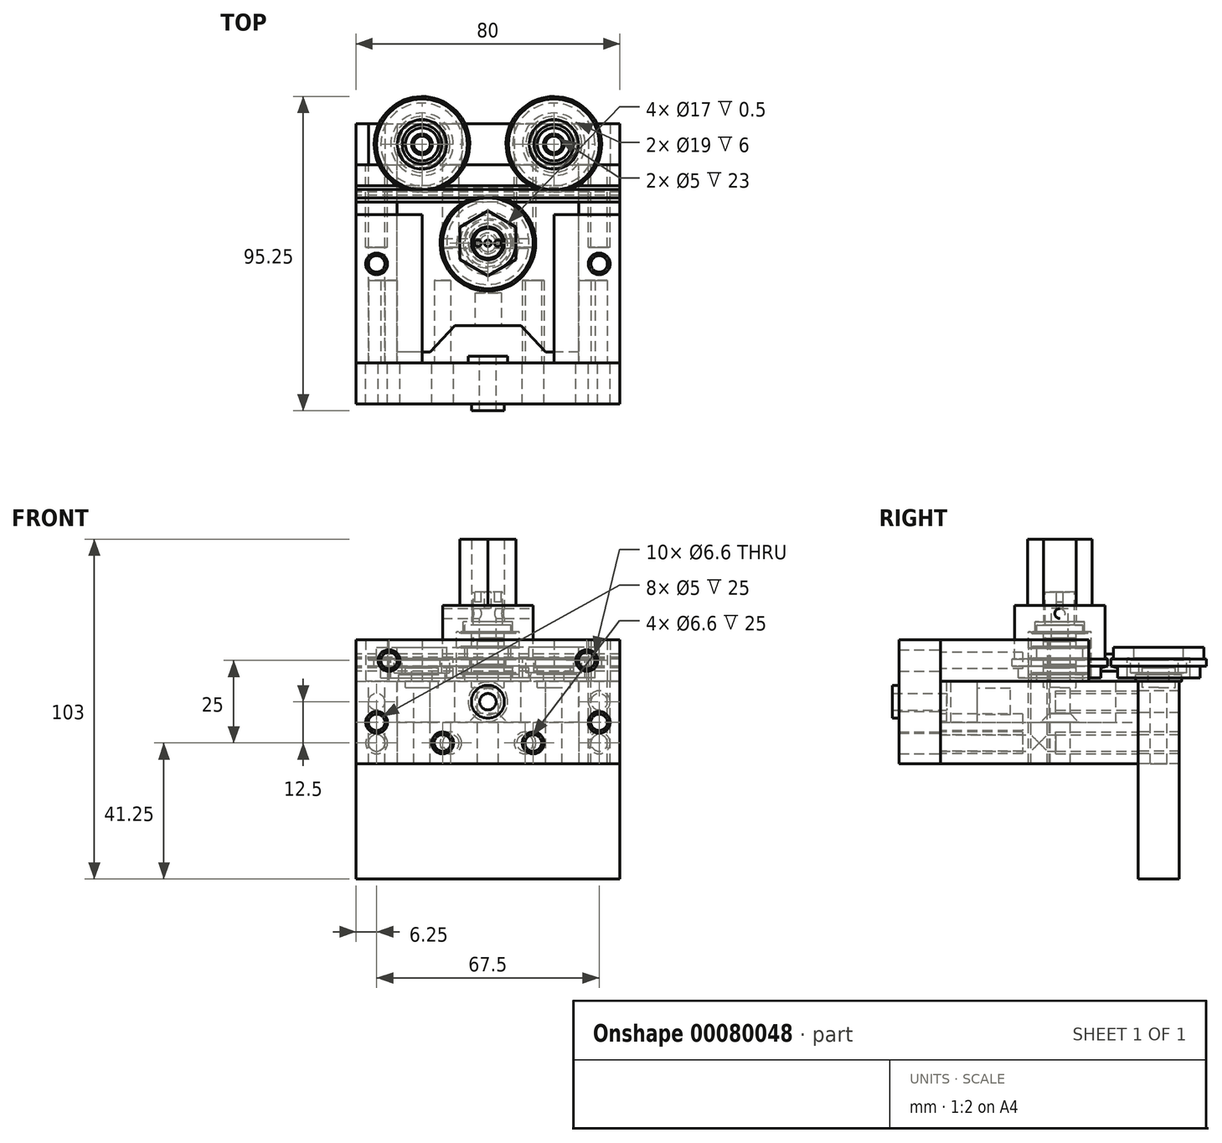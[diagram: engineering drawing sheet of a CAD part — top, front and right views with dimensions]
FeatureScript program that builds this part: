
annotation { "Feature Type Name" : "Feature", "Feature Type Description" : "" }
export const myFeature = defineFeature(function(context is Context, id is Id, definition is map)
    precondition{}
    {
        {
            assignVariable(context, id + "F0", {"name" : "M6clear", "anyValue" : 6.6});
        }
        {
            assignVariable(context, id + "F1", {"name" : "M6cap", "anyValue" : 12});
        }
        {
            var Q0;
            Q0=qCreatedBy(makeId("Top.planeOp"),FACE);
            var sketch = newSketch(context, id + "F2", { "sketchPlane" : qUnion([Q0])});
            skLineSegment(sketch, "E0.bottom", {"start": v(-40, 25) * mm, "end": v(40, 25) * mm});
            skLineSegment(sketch, "E1.top", {"start": v(-40, 37.5) * mm, "end": v(40, 37.5) * mm});
            skLineSegment(sketch, "E1.left", {"start": v(-40, 25) * mm, "end": v(-40, 37.5) * mm});
            skLineSegment(sketch, "E1.right", {"start": v(40, 25) * mm, "end": v(40, 37.5) * mm});
            skLineSegment(sketch, "E2", {"start": v(0, 25) * mm, "end": v(0, 37.5) * mm, "construction": true});
            skSolve(sketch);
        }
        {
            var Q0;
            Q0=makeQuery(id+"F2.imprint","IMPRINT",FACE,{"disambiguationData":[TD([[makeQuery(id+"F2.imprint","IMPRINT",EDGE,{"derivedFrom":sQuery(id+"F2.wireOp",EDGE,"E1.top")}),-1.0]])]});
            extrude(context, id + "F3", {"entities" : qUnion([Q0]), "oppositeDirection" : true, "depth" : 60 * mm});
        }
        {
            var Q0;
            Q0=qCreatedBy(makeId("Right.planeOp"),FACE);
            var sketch = newSketch(context, id + "F4", { "sketchPlane" : qUnion([Q0])});
            skLineSegment(sketch, "E3", {"start": v(13.75, 3) * mm, "end": v(18.75, 3) * mm});
            skLineSegment(sketch, "E4", {"start": v(18.75, 3) * mm, "end": v(18.75, 4) * mm});
            skLineSegment(sketch, "E5", {"start": v(18.75, 4) * mm, "end": v(16.75, 4.5) * mm});
            skLineSegment(sketch, "E6", {"start": v(16.75, 4.5) * mm, "end": v(16.75, 6.7) * mm});
            skLineSegment(sketch, "E7", {"start": v(16.75, 6.7) * mm, "end": v(17.5, 7.2) * mm});
            skLineSegment(sketch, "E8", {"start": v(17.5, 7.2) * mm, "end": v(17.5, 8.2) * mm});
            skLineSegment(sketch, "E9", {"start": v(17.5, 8.2) * mm, "end": v(15, 8.2) * mm});
            skLineSegment(sketch, "E10", {"start": v(15, 8.2) * mm, "end": v(15, 7.2) * mm});
            skLineSegment(sketch, "E11", {"start": v(15, 7.2) * mm, "end": v(15.75, 6.7) * mm});
            skLineSegment(sketch, "E12", {"start": v(15.75, 6.7) * mm, "end": v(15.75, 4.5) * mm});
            skLineSegment(sketch, "E13", {"start": v(15.75, 4.5) * mm, "end": v(13.75, 4) * mm});
            skLineSegment(sketch, "E14", {"start": v(13.75, 4) * mm, "end": v(13.75, 3) * mm});
            skLineSegment(sketch, "E15", {"start": v(17.5, 8.2) * mm, "end": v(17.5, 10.2) * mm});
            skLineSegment(sketch, "E16", {"start": v(17.5, 7.2) * mm, "end": v(17.5, 6.7) * mm});
            skLineSegment(sketch, "E17", {"start": v(17.5, 6.7) * mm, "end": v(16.75, 6.7) * mm});
            skLineSegment(sketch, "E18", {"start": v(16.75, 4.5) * mm, "end": v(18.75, 4.5) * mm});
            skLineSegment(sketch, "E19", {"start": v(18.75, 4.5) * mm, "end": v(18.75, 4) * mm});
            skLineSegment(sketch, "E20", {"start": v(18.75, 3) * mm, "end": v(18.75, 1) * mm});
            skLineSegment(sketch, "E21", {"start": v(15, 23) * mm, "end": v(15, 8.2) * mm});
            skLineSegment(sketch, "E22", {"start": v(15, 7.2) * mm, "end": v(15, 6.7) * mm});
            skLineSegment(sketch, "E23", {"start": v(15, 6.7) * mm, "end": v(15.75, 6.7) * mm});
            skLineSegment(sketch, "E24", {"start": v(15.75, 4.5) * mm, "end": v(13.75, 4.5) * mm});
            skLineSegment(sketch, "E25", {"start": v(13.75, 4.5) * mm, "end": v(13.75, 4) * mm});
            skLineSegment(sketch, "E26", {"start": v(13.75, 3) * mm, "end": v(13.75, 1) * mm});
            skLineSegment(sketch, "E27", {"start": v(18.75, 1) * mm, "end": v(21.75, 1) * mm});
            skLineSegment(sketch, "E28", {"start": v(21.75, 1) * mm, "end": v(21.75, 7) * mm});
            skLineSegment(sketch, "E29", {"start": v(21.75, 7) * mm, "end": v(23.75, 7) * mm});
            skLineSegment(sketch, "E30", {"start": v(23.75, 7) * mm, "end": v(23.75, 10.2) * mm});
            skLineSegment(sketch, "E31", {"start": v(23.75, 10.2) * mm, "end": v(17.5, 10.2) * mm});
            skLineSegment(sketch, "E32", {"start": v(31.25, 34.4) * mm, "end": v(31.25, 0) * mm, "construction": true});
            skLineSegment(sketch, "E33", {"start": v(13.75, 1) * mm, "end": v(10.75, 1) * mm});
            skLineSegment(sketch, "E34", {"start": v(10.75, 1) * mm, "end": v(10.75, 7) * mm});
            skLineSegment(sketch, "E35.bottom", {"start": v(21.75, 7) * mm, "end": v(22.75, 7) * mm});
            skLineSegment(sketch, "E35.top", {"start": v(21.75, 2) * mm, "end": v(22.75, 2) * mm});
            skLineSegment(sketch, "E35.left", {"start": v(21.75, 7) * mm, "end": v(21.75, 2) * mm});
            skLineSegment(sketch, "E35.right", {"start": v(22.75, 7) * mm, "end": v(22.75, 2) * mm});
            skLineSegment(sketch, "E36.bottom", {"start": v(25.25, 7) * mm, "end": v(26.25, 7) * mm});
            skLineSegment(sketch, "E36.top", {"start": v(25.25, 2) * mm, "end": v(26.25, 2) * mm});
            skLineSegment(sketch, "E36.left", {"start": v(25.25, 7) * mm, "end": v(25.25, 2) * mm});
            skLineSegment(sketch, "E36.right", {"start": v(26.25, 7) * mm, "end": v(26.25, 2) * mm});
            skLineSegment(sketch, "E37.bottom", {"start": v(25.25, 6.5) * mm, "end": v(22.75, 6.5) * mm});
            skLineSegment(sketch, "E37.top", {"start": v(25.25, 2.5) * mm, "end": v(22.75, 2.5) * mm});
            skLineSegment(sketch, "E37.left", {"start": v(25.25, 6.5) * mm, "end": v(25.25, 2.5) * mm});
            skLineSegment(sketch, "E37.right", {"start": v(22.75, 6.5) * mm, "end": v(22.75, 2.5) * mm});
            skLineSegment(sketch, "E38.bottom", {"start": v(10.75, 7) * mm, "end": v(9.75, 7) * mm});
            skLineSegment(sketch, "E38.top", {"start": v(10.75, 2) * mm, "end": v(9.75, 2) * mm});
            skLineSegment(sketch, "E38.left", {"start": v(10.75, 7) * mm, "end": v(10.75, 2) * mm});
            skLineSegment(sketch, "E38.right", {"start": v(9.75, 7) * mm, "end": v(9.75, 2) * mm});
            skLineSegment(sketch, "E39.bottom", {"start": v(7.25, 7) * mm, "end": v(6.25, 7) * mm});
            skLineSegment(sketch, "E39.top", {"start": v(7.25, 2) * mm, "end": v(6.25, 2) * mm});
            skLineSegment(sketch, "E39.left", {"start": v(7.25, 7) * mm, "end": v(7.25, 2) * mm});
            skLineSegment(sketch, "E39.right", {"start": v(6.25, 7) * mm, "end": v(6.25, 2) * mm});
            skLineSegment(sketch, "E40.bottom", {"start": v(9.75, 6.5) * mm, "end": v(7.25, 6.5) * mm});
            skLineSegment(sketch, "E40.top", {"start": v(9.75, 2.5) * mm, "end": v(7.25, 2.5) * mm});
            skLineSegment(sketch, "E40.left", {"start": v(9.75, 6.5) * mm, "end": v(9.75, 2.5) * mm});
            skLineSegment(sketch, "E40.right", {"start": v(7.25, 6.5) * mm, "end": v(7.25, 2.5) * mm});
            skLineSegment(sketch, "E41", {"start": v(1.25, 34.4) * mm, "end": v(1.25, 0) * mm, "construction": true});
            skLineSegment(sketch, "E42", {"start": v(6.25, 4) * mm, "end": v(4.4, 4) * mm});
            skLineSegment(sketch, "E43", {"start": v(4.4, 4) * mm, "end": v(4.4, -2) * mm});
            skLineSegment(sketch, "E44", {"start": v(8.25, 0) * mm, "end": v(8.25, 2) * mm});
            skLineSegment(sketch, "E45", {"start": v(8.25, 2) * mm, "end": v(6.25, 2) * mm});
            skLineSegment(sketch, "E46", {"start": v(26.25, 4) * mm, "end": v(28.1, 4) * mm});
            skLineSegment(sketch, "E47", {"start": v(28.1, 4) * mm, "end": v(28.1, -2) * mm});
            skLineSegment(sketch, "E48", {"start": v(24.25, 0) * mm, "end": v(24.25, 2) * mm});
            skLineSegment(sketch, "E49", {"start": v(24.25, 2) * mm, "end": v(26.25, 2) * mm});
            skLineSegment(sketch, "E50", {"start": v(8.75, 23) * mm, "end": v(15, 23) * mm});
            skLineSegment(sketch, "E51", {"start": v(8.75, 15) * mm, "end": v(8.75, 23) * mm});
            skLineSegment(sketch, "E52.bottom", {"start": v(9.75, 15) * mm, "end": v(10.75, 15) * mm});
            skLineSegment(sketch, "E52.top", {"start": v(9.75, 10) * mm, "end": v(10.75, 10) * mm});
            skLineSegment(sketch, "E52.left", {"start": v(9.75, 15) * mm, "end": v(9.75, 10) * mm});
            skLineSegment(sketch, "E52.right", {"start": v(10.75, 15) * mm, "end": v(10.75, 10) * mm});
            skLineSegment(sketch, "E53.bottom", {"start": v(6.25, 15) * mm, "end": v(7.25, 15) * mm});
            skLineSegment(sketch, "E53.top", {"start": v(6.25, 10) * mm, "end": v(7.25, 10) * mm});
            skLineSegment(sketch, "E53.left", {"start": v(6.25, 15) * mm, "end": v(6.25, 10) * mm});
            skLineSegment(sketch, "E53.right", {"start": v(7.25, 15) * mm, "end": v(7.25, 10) * mm});
            skLineSegment(sketch, "E54.bottom", {"start": v(7.25, 14.5) * mm, "end": v(9.75, 14.5) * mm});
            skLineSegment(sketch, "E54.top", {"start": v(7.25, 10.5) * mm, "end": v(9.75, 10.5) * mm});
            skLineSegment(sketch, "E54.left", {"start": v(7.25, 14.5) * mm, "end": v(7.25, 10.5) * mm});
            skLineSegment(sketch, "E54.right", {"start": v(9.75, 14.5) * mm, "end": v(9.75, 10.5) * mm});
            skLineSegment(sketch, "E55", {"start": v(4.4, 12) * mm, "end": v(4.4, 5) * mm});
            skLineSegment(sketch, "E56", {"start": v(4.4, 5) * mm, "end": v(6.25, 5) * mm});
            skLineSegment(sketch, "E57", {"start": v(6.25, 5) * mm, "end": v(6.25, 7) * mm});
            skLineSegment(sketch, "E58", {"start": v(7.25, 7) * mm, "end": v(8.25, 7) * mm});
            skLineSegment(sketch, "E59", {"start": v(8.25, 7) * mm, "end": v(8.25, 10) * mm});
            skLineSegment(sketch, "E60", {"start": v(8.25, 10) * mm, "end": v(7.25, 10) * mm});
            skLineSegment(sketch, "E61", {"start": v(4.4, 12) * mm, "end": v(6.25, 12) * mm});
            skLineSegment(sketch, "E62", {"start": v(7.25, 15) * mm, "end": v(8.25, 15) * mm});
            skLineSegment(sketch, "E63", {"start": v(8.25, 15) * mm, "end": v(8.25, 17) * mm});
            skLineSegment(sketch, "E64", {"start": v(8.25, 17) * mm, "end": v(5.75, 17) * mm});
            skLineSegment(sketch, "E65", {"start": v(3.75, 17) * mm, "end": v(3.75, 13) * mm});
            skLineSegment(sketch, "E66", {"start": v(3.75, 13) * mm, "end": v(6.25, 13) * mm});
            skLineSegment(sketch, "E67", {"start": v(10.75, 7) * mm, "end": v(10.75, 10) * mm});
            skLineSegment(sketch, "E68", {"start": v(9.75, 15) * mm, "end": v(8.75, 15) * mm});
            skLineSegment(sketch, "E69", {"start": v(16.25, 30.2) * mm, "end": v(16.25, 10.14) * mm, "construction": true});
            skLineSegment(sketch, "E70", {"start": v(8.25, 0) * mm, "end": v(6.25, 0) * mm});
            skLineSegment(sketch, "E71", {"start": v(6.25, 0) * mm, "end": v(6.25, -2) * mm});
            skLineSegment(sketch, "E72", {"start": v(6.25, -2) * mm, "end": v(4.4, -2) * mm});
            skLineSegment(sketch, "E73", {"start": v(24.25, 0) * mm, "end": v(26.25, 0) * mm});
            skLineSegment(sketch, "E74", {"start": v(26.25, 0) * mm, "end": v(26.25, -2) * mm});
            skLineSegment(sketch, "E75", {"start": v(26.25, -2) * mm, "end": v(28.1, -2) * mm});
            skLineSegment(sketch, "E76.top", {"start": v(1.25, 27) * mm, "end": v(5.75, 27) * mm});
            skLineSegment(sketch, "E76.right", {"start": v(5.75, 17) * mm, "end": v(5.75, 27) * mm});
            skLineSegment(sketch, "E77", {"start": v(1.25, 22) * mm, "end": v(3.75, 22) * mm});
            skLineSegment(sketch, "E78", {"start": v(1.25, 22) * mm, "end": v(1.25, 27) * mm});
            skLineSegment(sketch, "E79", {"start": v(3.75, 17) * mm, "end": v(3.75, 22) * mm});
            skSolve(sketch);
        }
        {
            var Q0;
            Q0=makeQuery(id+"F4.imprint","IMPRINT",FACE,{"disambiguationData":[TD([[makeQuery(id+"F4.imprint","IMPRINT",EDGE,{"derivedFrom":sQuery(id+"F4.wireOp",EDGE,"E4")}),-1.0]])]});
            var Q1;
            Q1=sQuery(id+"F4.wireOp",EDGE,"E32");
            revolve(context, id + "F5", {"entities" : qUnion([Q0]), "axis" : qUnion([Q1]), "revolveType" : RevolveType.FULL});
        }
        {
            var Q0;
            Q0=makeQuery(id+"F4.imprint","IMPRINT",FACE,{"disambiguationData":[TD([[makeQuery(id+"F4.imprint","IMPRINT",EDGE,{"derivedFrom":sQuery(id+"F4.wireOp",EDGE,"E3")}),1.0]])]});
            var Q1;
            Q1=makeQuery(id+"F3.opExtrude","SWEPT_FACE",FACE,{"disambiguationData":[OSD([sQuery(id+"F2.wireOp",EDGE,"E1.right")])]});
            var Q2;
            Q2=makeQuery(id+"F3.opExtrude","SWEPT_FACE",FACE,{"disambiguationData":[OSD([sQuery(id+"F2.wireOp",EDGE,"E1.left")])]});
            extrude(context, id + "F6", {"entities" : qUnion([Q0]), "endBound" : BoundingType.UP_TO_SURFACE, "endBoundEntityFace" : qUnion([Q1]), "depth" : 25 * mm, "hasSecondDirection" : true, "secondDirectionBound" : SecondDirectionBoundingType.UP_TO_SURFACE, "secondDirectionOppositeDirection" : true, "secondDirectionBoundEntityFace" : qUnion([Q2]), "secondDirectionDepth" : 25 * mm});
        }
        {
            var Q0;
            {var subQ7=sQuery(id+"F4.wireOp",EDGE,"E37.left");Q0=makeQuery(id+"F4.imprint","IMPRINT",FACE,{"disambiguationData":[TD([[makeQuery(id+"F4.imprint","IMPRINT",EDGE,{"derivedFrom":subQ7}),1.0]])]});}
            var Q1;
            Q1=makeQuery(id+"F4.imprint","IMPRINT",FACE,{"disambiguationData":[TD([[makeQuery(id+"F4.imprint","IMPRINT",EDGE,{"derivedFrom":sQuery(id+"F4.wireOp",EDGE,"E37.bottom")}),1.0]])]});
            var Q2;
            {var subQ1=sQuery(id+"F4.wireOp",EDGE,"E35.bottom");Q2=makeQuery(id+"F4.imprint","IMPRINT",FACE,{"disambiguationData":[TD([[makeQuery(id+"F4.imprint","IMPRINT",EDGE,{"derivedFrom":subQ1}),-1.0]])]});}
            var Q3;
            Q3=sQuery(id+"F4.wireOp",EDGE,"E32");
            revolve(context, id + "F7", {"entities" : qUnion([Q0, Q1, Q2]), "axis" : qUnion([Q3]), "revolveType" : RevolveType.FULL});
        }
        {
            var Q0;
            Q0=makeQuery(id+"F4.imprint","IMPRINT",FACE,{"disambiguationData":[TD([[makeQuery(id+"F4.imprint","IMPRINT",EDGE,{"derivedFrom":sQuery(id+"F4.wireOp",EDGE,"E10")}),-1.0]])]});
            var Q1;
            Q1=sQuery(id+"F4.wireOp",EDGE,"E41");
            revolve(context, id + "F8", {"entities" : qUnion([Q0]), "axis" : qUnion([Q1]), "revolveType" : RevolveType.FULL});
        }
        {
            var Q0;
            {var subQ1=sQuery(id+"F4.wireOp",EDGE,"E38.bottom");Q0=makeQuery(id+"F4.imprint","IMPRINT",FACE,{"disambiguationData":[TD([[makeQuery(id+"F4.imprint","IMPRINT",EDGE,{"derivedFrom":subQ1}),1.0]])]});}
            var Q1;
            Q1=makeQuery(id+"F4.imprint","IMPRINT",FACE,{"disambiguationData":[TD([[makeQuery(id+"F4.imprint","IMPRINT",EDGE,{"derivedFrom":sQuery(id+"F4.wireOp",EDGE,"E40.bottom")}),1.0]])]});
            var Q2;
            {var subQ3=sQuery(id+"F4.wireOp",EDGE,"E39.bottom");Q2=makeQuery(id+"F4.imprint","IMPRINT",FACE,{"disambiguationData":[TD([[makeQuery(id+"F4.imprint","IMPRINT",EDGE,{"derivedFrom":subQ3}),1.0]])]});}
            var Q3;
            {var subQ3=sQuery(id+"F4.wireOp",EDGE,"E53.bottom");Q3=makeQuery(id+"F4.imprint","IMPRINT",FACE,{"disambiguationData":[TD([[makeQuery(id+"F4.imprint","IMPRINT",EDGE,{"derivedFrom":subQ3}),-1.0]])]});}
            var Q4;
            Q4=makeQuery(id+"F4.imprint","IMPRINT",FACE,{"disambiguationData":[TD([[makeQuery(id+"F4.imprint","IMPRINT",EDGE,{"derivedFrom":sQuery(id+"F4.wireOp",EDGE,"E54.bottom")}),-1.0]])]});
            var Q5;
            {var subQ3=sQuery(id+"F4.wireOp",EDGE,"E52.bottom");Q5=makeQuery(id+"F4.imprint","IMPRINT",FACE,{"disambiguationData":[TD([[makeQuery(id+"F4.imprint","IMPRINT",EDGE,{"derivedFrom":subQ3}),-1.0]])]});}
            var Q6;
            Q6=sQuery(id+"F4.wireOp",EDGE,"E41");
            revolve(context, id + "F9", {"entities" : qUnion([Q0, Q1, Q2, Q3, Q4, Q5]), "axis" : qUnion([Q6]), "revolveType" : RevolveType.FULL});
        }
        {
            var Q0;
            {var subQ4=sQuery(id+"F4.wireOp",EDGE,"E42");Q0=makeQuery(id+"F4.imprint","IMPRINT",FACE,{"disambiguationData":[TD([[makeQuery(id+"F4.imprint","IMPRINT",EDGE,{"derivedFrom":subQ4}),1.0]])]});}
            var Q1;
            Q1=makeQuery(id+"F4.imprint","IMPRINT",FACE,{"disambiguationData":[TD([[makeQuery(id+"F4.imprint","IMPRINT",EDGE,{"derivedFrom":sQuery(id+"F4.wireOp",EDGE,"E39.bottom")}),-1.0]])]});
            var Q2;
            {var subQ1=sQuery(id+"F4.wireOp",EDGE,"E53.bottom");Q2=makeQuery(id+"F4.imprint","IMPRINT",FACE,{"disambiguationData":[TD([[makeQuery(id+"F4.imprint","IMPRINT",EDGE,{"derivedFrom":subQ1}),1.0]])]});}
            var Q3;
            Q3=sQuery(id+"F4.wireOp",EDGE,"E41");
            revolve(context, id + "F10", {"entities" : qUnion([Q0, Q1, Q2]), "axis" : qUnion([Q3]), "revolveType" : RevolveType.FULL});
        }
        {
            var Q0;
            {var subQ3=sQuery(id+"F4.wireOp",EDGE,"E46");Q0=makeQuery(id+"F4.imprint","IMPRINT",FACE,{"disambiguationData":[TD([[makeQuery(id+"F4.imprint","IMPRINT",EDGE,{"derivedFrom":subQ3}),-1.0]])]});}
            var Q1;
            Q1=makeQuery(id+"F4.imprint","IMPRINT",FACE,{"disambiguationData":[TD([[makeQuery(id+"F4.imprint","IMPRINT",EDGE,{"derivedFrom":sQuery(id+"F4.wireOp",EDGE,"NxfEYC14-Hdi1-JHQ3-9HRZ-zY9b5y3UeP3D")}),1.0]])]});
            var Q2;
            Q2=sQuery(id+"F4.wireOp",EDGE,"E32");
            revolve(context, id + "F11", {"entities" : qUnion([Q0, Q1]), "axis" : qUnion([Q2]), "revolveType" : RevolveType.FULL});
        }
        {
            var Q0;
            Q0=makeQuery(id+"F8.opRevolve","SWEPT_FACE",FACE,{"disambiguationData":[OSD([sQuery(id+"F4.wireOp",EDGE,"E50")])]});
            var sketch = newSketch(context, id + "F12", { "sketchPlane" : qUnion([Q0])});
            skLineSegment(sketch, "E80", {"start": v(0, -12.5) * mm, "end": v(0, 15) * mm, "construction": true});
            skPoint(sketch, "E81", {"position": v(0, 1.25) * mm});
            skCircle(sketch, "E82.cCircle", {"center": v(0, 1.25) * mm, "radius": 8.5 * mm, "construction": true});
            skLineSegment(sketch, "E82.0", {"start": v(-8.5, 6.16) * mm, "end": v(0, 11.06) * mm});
            skLineSegment(sketch, "E82.1", {"start": v(0, 11.06) * mm, "end": v(8.5, 6.16) * mm});
            skLineSegment(sketch, "E82.2", {"start": v(8.5, 6.16) * mm, "end": v(8.5, -3.66) * mm});
            skLineSegment(sketch, "E82.3", {"start": v(8.5, -3.66) * mm, "end": v(0, -8.56) * mm});
            skLineSegment(sketch, "E82.4", {"start": v(0, -8.56) * mm, "end": v(-8.5, -3.66) * mm});
            skLineSegment(sketch, "E82.5", {"start": v(-8.5, -3.66) * mm, "end": v(-8.5, 6.16) * mm});
            skPoint(sketch, "E82.0.midPoint", {"position": v(-4.25, 8.61) * mm});
            skCircle(sketch, "E83", {"center": v(0, 1.25) * mm, "radius": 5 * mm});
            skSolve(sketch);
        }
        {
            var Q0;
            Q0=makeQuery(id+"F12.imprint","IMPRINT",FACE,{"disambiguationData":[TD([[makeQuery(id+"F12.imprint","IMPRINT",EDGE,{"derivedFrom":sQuery(id+"F12.wireOp",EDGE,"E82.0")}),-1.0]])]});
            var Q1;
            Q1=makeQuery(id+"F12.imprint","IMPRINT",FACE,{"disambiguationData":[TD([[makeQuery(id+"F12.imprint","IMPRINT",EDGE,{"derivedFrom":makeQuery(id+"F8.opRevolve","SWEPT_EDGE",EDGE,{"disambiguationData":[OSD([sQuery(id+"F4.wireOp",EDGE,"uuJSe70I-DSXr-Ou4z-5Yxw-1lKSFgM0PJ0F"),sQuery(id+"F4.wireOp",EDGE,"E50")])]})}),1.0]])]});
            extrude(context, id + "F13", {"entities" : qUnion([Q0, Q1]), "depth" : 20 * mm});
        }
        {
            var Q0;
            Q0=makeQuery(id+"F12.imprint","IMPRINT",FACE,{"disambiguationData":[TD([[makeQuery(id+"F12.imprint","IMPRINT",EDGE,{"derivedFrom":makeQuery(id+"F8.opRevolve","SWEPT_EDGE",EDGE,{"disambiguationData":[OSD([sQuery(id+"F4.wireOp",EDGE,"E50"),sQuery(id+"F4.wireOp",EDGE,"E51")])]})}),1.0]])]});
            var Q1;
            Q1=makeQuery(id+"F13.opExtrude","CAP_FACE",FACE,{"disambiguationData":[OSD([sQuery(id+"F12.wireOp",EDGE,"E82.0"),sQuery(id+"F12.wireOp",EDGE,"E82.1"),sQuery(id+"F12.wireOp",EDGE,"E82.2"),sQuery(id+"F12.wireOp",EDGE,"E82.3"),sQuery(id+"F12.wireOp",EDGE,"E82.4"),sQuery(id+"F12.wireOp",EDGE,"E82.5")])],"isStart":false});
            extrude(context, id + "F14", {"entities" : qUnion([Q0]), "operationType" : NewBodyOperationType.ADD, "oppositeDirection" : true, "endBoundEntityFace" : qUnion([Q1]), "depth" : 5 * mm});
        }
        {
            var Q0;
            Q0=makeQuery(id+"F5.opRevolve","SWEPT_BODY",BODY,{"disambiguationData":[OSD([sQuery(id+"F4.wireOp",EDGE,"E4"),sQuery(id+"F4.wireOp",EDGE,"E6"),sQuery(id+"F4.wireOp",EDGE,"E8"),sQuery(id+"F4.wireOp",EDGE,"E15"),sQuery(id+"F4.wireOp",EDGE,"E16"),sQuery(id+"F4.wireOp",EDGE,"E17"),sQuery(id+"F4.wireOp",EDGE,"E18"),sQuery(id+"F4.wireOp",EDGE,"E19"),sQuery(id+"F4.wireOp",EDGE,"E20"),sQuery(id+"F4.wireOp",EDGE,"E27"),sQuery(id+"F4.wireOp",EDGE,"E28"),sQuery(id+"F4.wireOp",EDGE,"E29"),sQuery(id+"F4.wireOp",EDGE,"E30"),sQuery(id+"F4.wireOp",EDGE,"E31"),sQuery(id+"F4.wireOp",EDGE,"E35.bottom"),sQuery(id+"F4.wireOp",EDGE,"E35.left")])]});
            var Q1;
            Q1=makeQuery(id+"F11.opRevolve","SWEPT_BODY",BODY,{"disambiguationData":[OSD([sQuery(id+"F4.wireOp",EDGE,"NxfEYC14-Hdi1-JHQ3-9HRZ-zY9b5y3UeP3D"),sQuery(id+"F4.wireOp",EDGE,"drXEmD9R-yPd3-h9GW-ujEZ-zWC1Y2sE0ly5"),sQuery(id+"F4.wireOp",EDGE,"mZtHpLO8-qHN3-iVYr-RRkK-fKMUtDvmlHCf"),sQuery(id+"F4.wireOp",EDGE,"nrruY4Ww-LVbw-ZvRd-GPQl-C1fDlobpOkn2"),sQuery(id+"F4.wireOp",EDGE,"zwKcQELd-qS3u-5nsg-Vl8e-YyjTL161zu4a"),sQuery(id+"F4.wireOp",EDGE,"jR6KMhXO-00QE-dQdN-2mNZ-AHTwbRT6lp6G")])]});
            var Q2;
            Q2=makeQuery(id+"F7.opRevolve","SWEPT_BODY",BODY,{"disambiguationData":[OSD([sQuery(id+"F4.wireOp",EDGE,"E35.bottom"),sQuery(id+"F4.wireOp",EDGE,"E35.top"),sQuery(id+"F4.wireOp",EDGE,"E35.left"),sQuery(id+"F4.wireOp",EDGE,"E35.right"),sQuery(id+"F4.wireOp",EDGE,"E37.bottom"),sQuery(id+"F4.wireOp",EDGE,"E37.top"),sQuery(id+"F4.wireOp",EDGE,"E37.left")])]});
            var Q3;
            Q3=makeQuery(id+"F11.opRevolve","SWEPT_BODY",BODY,{"disambiguationData":[OSD([sQuery(id+"F4.wireOp",EDGE,"E36.right"),sQuery(id+"F4.wireOp",EDGE,"E46"),sQuery(id+"F4.wireOp",EDGE,"E47"),sQuery(id+"F4.wireOp",EDGE,"E48"),sQuery(id+"F4.wireOp",EDGE,"E49"),sQuery(id+"F4.wireOp",EDGE,"E73"),sQuery(id+"F4.wireOp",EDGE,"E74"),sQuery(id+"F4.wireOp",EDGE,"E75")])]});
            var Q4;
            Q4=makeQuery(id+"F3.opExtrude","CAP_EDGE",EDGE,{"disambiguationData":[OSD([sQuery(id+"F2.wireOp",EDGE,"E0.bottom")])],"isStart":true});
            transform(context, id + "F15", {"entities" : qUnion([Q0, Q1, Q2, Q3]), "transformType" : TransformType.TRANSLATION_DISTANCE, "transformDirection" : qUnion([Q4]), "distance" : 20 * mm, "makeCopy" : false});
        }
        {
            var Q0;
            Q0=makeQuery(id+"F5.opRevolve","SWEPT_BODY",BODY,{"disambiguationData":[OSD([sQuery(id+"F4.wireOp",EDGE,"E4"),sQuery(id+"F4.wireOp",EDGE,"E6"),sQuery(id+"F4.wireOp",EDGE,"E8"),sQuery(id+"F4.wireOp",EDGE,"E15"),sQuery(id+"F4.wireOp",EDGE,"E16"),sQuery(id+"F4.wireOp",EDGE,"E17"),sQuery(id+"F4.wireOp",EDGE,"E18"),sQuery(id+"F4.wireOp",EDGE,"E19"),sQuery(id+"F4.wireOp",EDGE,"E20"),sQuery(id+"F4.wireOp",EDGE,"E27"),sQuery(id+"F4.wireOp",EDGE,"E28"),sQuery(id+"F4.wireOp",EDGE,"E29"),sQuery(id+"F4.wireOp",EDGE,"E30"),sQuery(id+"F4.wireOp",EDGE,"E31"),sQuery(id+"F4.wireOp",EDGE,"E35.bottom"),sQuery(id+"F4.wireOp",EDGE,"E35.left")])]});
            var Q1;
            Q1=makeQuery(id+"F11.opRevolve","SWEPT_BODY",BODY,{"disambiguationData":[OSD([sQuery(id+"F4.wireOp",EDGE,"NxfEYC14-Hdi1-JHQ3-9HRZ-zY9b5y3UeP3D"),sQuery(id+"F4.wireOp",EDGE,"drXEmD9R-yPd3-h9GW-ujEZ-zWC1Y2sE0ly5"),sQuery(id+"F4.wireOp",EDGE,"mZtHpLO8-qHN3-iVYr-RRkK-fKMUtDvmlHCf"),sQuery(id+"F4.wireOp",EDGE,"nrruY4Ww-LVbw-ZvRd-GPQl-C1fDlobpOkn2"),sQuery(id+"F4.wireOp",EDGE,"zwKcQELd-qS3u-5nsg-Vl8e-YyjTL161zu4a"),sQuery(id+"F4.wireOp",EDGE,"jR6KMhXO-00QE-dQdN-2mNZ-AHTwbRT6lp6G")])]});
            var Q2;
            Q2=makeQuery(id+"F7.opRevolve","SWEPT_BODY",BODY,{"disambiguationData":[OSD([sQuery(id+"F4.wireOp",EDGE,"E35.bottom"),sQuery(id+"F4.wireOp",EDGE,"E35.top"),sQuery(id+"F4.wireOp",EDGE,"E35.left"),sQuery(id+"F4.wireOp",EDGE,"E35.right"),sQuery(id+"F4.wireOp",EDGE,"E37.bottom"),sQuery(id+"F4.wireOp",EDGE,"E37.top"),sQuery(id+"F4.wireOp",EDGE,"E37.left")])]});
            var Q3;
            Q3=makeQuery(id+"F11.opRevolve","SWEPT_BODY",BODY,{"disambiguationData":[OSD([sQuery(id+"F4.wireOp",EDGE,"E36.right"),sQuery(id+"F4.wireOp",EDGE,"E46"),sQuery(id+"F4.wireOp",EDGE,"E47"),sQuery(id+"F4.wireOp",EDGE,"E48"),sQuery(id+"F4.wireOp",EDGE,"E49"),sQuery(id+"F4.wireOp",EDGE,"E73"),sQuery(id+"F4.wireOp",EDGE,"E74"),sQuery(id+"F4.wireOp",EDGE,"E75")])]});
            var Q4;
            Q4=qCreatedBy(makeId("Right.planeOp"),FACE);
            mirror(context, id + "F16", {"entities" : qUnion([Q0, Q1, Q2, Q3]), "mirrorPlane" : qUnion([Q4])});
        }
        {
            var Q0;
            Q0=makeQuery(id+"F3.opExtrude","SWEPT_FACE",FACE,{"disambiguationData":[OSD([sQuery(id+"F2.wireOp",EDGE,"E0.bottom")])]});
            var sketch = newSketch(context, id + "F17", { "sketchPlane" : qUnion([Q0])});
            skLineSegment(sketch, "E84.bottom", {"start": v(-40, 0) * mm, "end": v(-27.5, 0) * mm});
            skLineSegment(sketch, "E84.top", {"start": v(-40, -25) * mm, "end": v(-27.5, -25) * mm});
            skLineSegment(sketch, "E84.left", {"start": v(-40, 0) * mm, "end": v(-40, -25) * mm});
            skLineSegment(sketch, "E84.right", {"start": v(-27.5, 0) * mm, "end": v(-27.5, -25) * mm});
            skLineSegment(sketch, "E85.bottom", {"start": v(40, 0) * mm, "end": v(27.5, 0) * mm});
            skLineSegment(sketch, "E85.top", {"start": v(40, -25) * mm, "end": v(27.5, -25) * mm});
            skLineSegment(sketch, "E85.left", {"start": v(40, 0) * mm, "end": v(40, -25) * mm});
            skLineSegment(sketch, "E85.right", {"start": v(27.5, 0) * mm, "end": v(27.5, -25) * mm});
            skLineSegment(sketch, "E86.bottom", {"start": v(-27.5, -12.5) * mm, "end": v(27.5, -12.5) * mm});
            skLineSegment(sketch, "E86.top", {"start": v(-27.5, -25) * mm, "end": v(27.5, -25) * mm});
            skLineSegment(sketch, "E86.left", {"start": v(-27.5, -12.5) * mm, "end": v(-27.5, -25) * mm});
            skLineSegment(sketch, "E86.right", {"start": v(27.5, -12.5) * mm, "end": v(27.5, -25) * mm});
            skCircle(sketch, "E87", {"center": v(-33.75, -6.25) * mm, "radius": 2.5 * mm});
            skCircle(sketch, "E88", {"center": v(-33.75, -6.25) * mm, "radius": 3.3 * mm});
            skLineSegment(sketch, "E89", {"start": v(-40, 0) * mm, "end": v(-27.5, -12.5) * mm, "construction": true});
            skCircle(sketch, "E90.MirrorC", {"center": v(-33.75, -18.75) * mm, "radius": 3.3 * mm});
            skCircle(sketch, "E91.MirrorC", {"center": v(-33.75, -18.75) * mm, "radius": 2.5 * mm});
            skCircle(sketch, "E92.MirrorC", {"center": v(33.75, -6.25) * mm, "radius": 2.5 * mm});
            skCircle(sketch, "E93.MirrorC", {"center": v(33.75, -6.25) * mm, "radius": 3.3 * mm});
            skCircle(sketch, "E94.MirrorC", {"center": v(33.75, -18.75) * mm, "radius": 3.3 * mm});
            skCircle(sketch, "E95.MirrorC", {"center": v(33.75, -18.75) * mm, "radius": 2.5 * mm});
            skLineSegment(sketch, "E96", {"start": v(0, -12.5) * mm, "end": v(0, -25) * mm, "construction": true});
            skCircle(sketch, "E97", {"center": v(-11.25, -18.75) * mm, "radius": 2.5 * mm});
            skCircle(sketch, "E98", {"center": v(-11.25, -18.75) * mm, "radius": 3.3 * mm});
            skCircle(sketch, "E99.MirrorC", {"center": v(11.25, -18.75) * mm, "radius": 2.5 * mm});
            skCircle(sketch, "E100.MirrorC", {"center": v(11.25, -18.75) * mm, "radius": 3.3 * mm});
            skLineSegment(sketch, "E101", {"start": v(33.75, -18.75) * mm, "end": v(11.25, -18.75) * mm, "construction": true});
            skLineSegment(sketch, "E102", {"start": v(11.25, -18.75) * mm, "end": v(-11.25, -18.75) * mm, "construction": true});
            skSolve(sketch);
        }
        {
            var Q0;
            {var subQ1=sQuery(id+"F17.wireOp",EDGE,"E84.bottom");Q0=makeQuery(id+"F17.imprint","IMPRINT",FACE,{"disambiguationData":[TD([[makeQuery(id+"F17.imprint","IMPRINT",EDGE,{"derivedFrom":subQ1}),-1.0]])]});}
            var Q1;
            {var subQ1=sQuery(id+"F17.wireOp",EDGE,"E85.bottom");Q1=makeQuery(id+"F17.imprint","IMPRINT",FACE,{"disambiguationData":[TD([[makeQuery(id+"F17.imprint","IMPRINT",EDGE,{"derivedFrom":subQ1}),-1.0]])]});}
            var Q2;
            Q2=makeQuery(id+"F17.imprint","IMPRINT",FACE,{"disambiguationData":[TD([[makeQuery(id+"F17.imprint","IMPRINT",EDGE,{"derivedFrom":sQuery(id+"F17.wireOp",EDGE,"E91.MirrorC")}),-1.0]])]});
            var Q3;
            Q3=makeQuery(id+"F17.imprint","IMPRINT",FACE,{"disambiguationData":[TD([[makeQuery(id+"F17.imprint","IMPRINT",EDGE,{"derivedFrom":sQuery(id+"F17.wireOp",EDGE,"E90.MirrorC")}),-1.0]])]});
            var Q4;
            Q4=makeQuery(id+"F17.imprint","IMPRINT",FACE,{"disambiguationData":[TD([[makeQuery(id+"F17.imprint","IMPRINT",EDGE,{"derivedFrom":sQuery(id+"F17.wireOp",EDGE,"E87")}),-1.0]])]});
            var Q5;
            Q5=makeQuery(id+"F17.imprint","IMPRINT",FACE,{"disambiguationData":[TD([[makeQuery(id+"F17.imprint","IMPRINT",EDGE,{"derivedFrom":sQuery(id+"F17.wireOp",EDGE,"E87")}),1.0]])]});
            var Q6;
            Q6=makeQuery(id+"F17.imprint","IMPRINT",FACE,{"disambiguationData":[TD([[makeQuery(id+"F17.imprint","IMPRINT",EDGE,{"derivedFrom":sQuery(id+"F17.wireOp",EDGE,"E94.MirrorC")}),1.0]])]});
            var Q7;
            Q7=makeQuery(id+"F17.imprint","IMPRINT",FACE,{"disambiguationData":[TD([[makeQuery(id+"F17.imprint","IMPRINT",EDGE,{"derivedFrom":sQuery(id+"F17.wireOp",EDGE,"E95.MirrorC")}),1.0]])]});
            var Q8;
            Q8=makeQuery(id+"F17.imprint","IMPRINT",FACE,{"disambiguationData":[TD([[makeQuery(id+"F17.imprint","IMPRINT",EDGE,{"derivedFrom":sQuery(id+"F17.wireOp",EDGE,"E92.MirrorC")}),1.0]])]});
            var Q9;
            Q9=makeQuery(id+"F17.imprint","IMPRINT",FACE,{"disambiguationData":[TD([[makeQuery(id+"F17.imprint","IMPRINT",EDGE,{"derivedFrom":sQuery(id+"F17.wireOp",EDGE,"E92.MirrorC")}),-1.0]])]});
            extrude(context, id + "F18", {"entities" : qUnion([Q0, Q1, Q2, Q3, Q4, Q5, Q6, Q7, Q8, Q9]), "depth" : 60 * mm});
        }
        {
            var Q0;
            Q0=makeQuery(id+"F17.imprint","IMPRINT",FACE,{"disambiguationData":[TD([[makeQuery(id+"F17.imprint","IMPRINT",EDGE,{"derivedFrom":sQuery(id+"F17.wireOp",EDGE,"E86.bottom")}),-1.0]])]});
            var Q1;
            Q1=makeQuery(id+"F17.imprint","IMPRINT",FACE,{"disambiguationData":[TD([[makeQuery(id+"F17.imprint","IMPRINT",EDGE,{"derivedFrom":sQuery(id+"F17.wireOp",EDGE,"E99.MirrorC")}),-1.0]])]});
            var Q2;
            Q2=makeQuery(id+"F17.imprint","IMPRINT",FACE,{"disambiguationData":[TD([[makeQuery(id+"F17.imprint","IMPRINT",EDGE,{"derivedFrom":sQuery(id+"F17.wireOp",EDGE,"E99.MirrorC")}),1.0]])]});
            var Q3;
            Q3=makeQuery(id+"F17.imprint","IMPRINT",FACE,{"disambiguationData":[TD([[makeQuery(id+"F17.imprint","IMPRINT",EDGE,{"derivedFrom":sQuery(id+"F17.wireOp",EDGE,"jnnbCi9O-ACNy-IIGJ-mOF9-m1iE8Juj3V3K")}),-1.0]])]});
            var Q4;
            Q4=makeQuery(id+"F17.imprint","IMPRINT",FACE,{"disambiguationData":[TD([[makeQuery(id+"F17.imprint","IMPRINT",EDGE,{"derivedFrom":sQuery(id+"F17.wireOp",EDGE,"jnnbCi9O-ACNy-IIGJ-mOF9-m1iE8Juj3V3K")}),1.0]])]});
            var Q5;
            Q5=makeQuery(id+"F17.imprint","IMPRINT",FACE,{"disambiguationData":[TD([[makeQuery(id+"F17.imprint","IMPRINT",EDGE,{"derivedFrom":sQuery(id+"F17.wireOp",EDGE,"E97")}),-1.0]])]});
            var Q6;
            Q6=makeQuery(id+"F17.imprint","IMPRINT",FACE,{"disambiguationData":[TD([[makeQuery(id+"F17.imprint","IMPRINT",EDGE,{"derivedFrom":sQuery(id+"F17.wireOp",EDGE,"E97")}),1.0]])]});
            var Q7;
            Q7=makeQuery(id+"F18.opExtrude","CAP_FACE",FACE,{"disambiguationData":[OSD([sQuery(id+"F17.wireOp",EDGE,"E84.bottom"),sQuery(id+"F17.wireOp",EDGE,"E84.top"),sQuery(id+"F17.wireOp",EDGE,"E84.left"),sQuery(id+"F17.wireOp",EDGE,"E84.right"),sQuery(id+"F17.wireOp",EDGE,"E86.left")])],"isStart":false});
            extrude(context, id + "F19", {"entities" : qUnion([Q0, Q1, Q2, Q3, Q4, Q5, Q6]), "endBound" : BoundingType.UP_TO_SURFACE, "endBoundEntityFace" : qUnion([Q7]), "depth" : 25 * mm});
        }
        {
            var Q0;
            Q0=qCreatedBy(makeId("Top.planeOp"),FACE);
            var sketch = newSketch(context, id + "F20", { "sketchPlane" : qUnion([Q0])});
            skLineSegment(sketch, "E103.right", {"start": v(-27.5, -31.75) * mm, "end": v(-27.5, 18.25) * mm});
            skLineSegment(sketch, "E104", {"start": v(-27.5, 18.25) * mm, "end": v(27.5, 18.25) * mm});
            skLineSegment(sketch, "E105", {"start": v(27.5, -31.75) * mm, "end": v(27.5, 18.25) * mm});
            skLineSegment(sketch, "E106", {"start": v(0, 18.25) * mm, "end": v(0, -23.75) * mm, "construction": true});
            skPoint(sketch, "E107", {"position": v(0, 1.25) * mm});
            skLineSegment(sketch, "E108", {"start": v(27.5, -31.75) * mm, "end": v(17.5, -31.75) * mm});
            skLineSegment(sketch, "E109", {"start": v(17.5, -31.75) * mm, "end": v(10, -23.75) * mm});
            skLineSegment(sketch, "E110", {"start": v(10, -23.75) * mm, "end": v(-10, -23.75) * mm});
            skLineSegment(sketch, "E111", {"start": v(-10, -23.75) * mm, "end": v(-17.5, -31.75) * mm});
            skLineSegment(sketch, "E112", {"start": v(-17.5, -31.75) * mm, "end": v(-27.5, -31.75) * mm});
            skSolve(sketch);
        }
        {
            var Q0;
            {var subQ6=sQuery(id+"F20.wireOp",EDGE,"E103.right");Q0=makeQuery(id+"F20.imprint","IMPRINT",FACE,{"disambiguationData":[TD([[makeQuery(id+"F20.imprint","IMPRINT",EDGE,{"derivedFrom":subQ6}),-1.0]])]});}
            var Q1;
            Q1=makeQuery(id+"F20.imprint","IMPRINT",FACE,{"disambiguationData":[TD([[makeQuery(id+"F20.imprint","IMPRINT",EDGE,{"derivedFrom":sQuery(id+"F20.wireOp",EDGE,"dbzBGA0j-ETXt-6MKK-BUa3-G9SU3pradxuU")}),-1.0]])]});
            var Q2;
            {var subQ0=sQuery(id+"F20.wireOp",EDGE,"NvKQAOos-H9cN-pGW5-Qkrs-JOJb7hA8DHyl");var subQ1=makeQuery(id+"F20.imprint","INTERSECT",VERTEX,{"derivedFrom":[sQuery(id+"F20.wireOp",EDGE,"E105"),subQ0]});Q2=makeQuery(id+"F20.imprint","IMPRINT",FACE,{"disambiguationData":[TD([[makeQuery(id+"F20.imprint","IMPRINT",EDGE,{"disambiguationData":[TD([[subQ1,-1.0]])],"derivedFrom":subQ0}),1.0]])]});}
            var Q3;
            {var subQ0=sQuery(id+"F20.wireOp",EDGE,"hUwWPvgh-PofT-npAS-kujz-laP0mAycR8kE");var subQ1=makeQuery(id+"F20.imprint","INTERSECT",VERTEX,{"derivedFrom":[sQuery(id+"F20.wireOp",EDGE,"E103.right"),subQ0]});Q3=makeQuery(id+"F20.imprint","IMPRINT",FACE,{"disambiguationData":[TD([[makeQuery(id+"F20.imprint","IMPRINT",EDGE,{"disambiguationData":[TD([[subQ1,-1.0]])],"derivedFrom":subQ0}),1.0]])]});}
            extrude(context, id + "F21", {"entities" : qUnion([Q0, Q1, Q2, Q3]), "oppositeDirection" : true, "depth" : 12.5 * mm});
        }
        {
            var Q0;
            Q0=makeQuery(id+"F18.opExtrude","SWEPT_FACE",FACE,{"disambiguationData":[OSD([sQuery(id+"F17.wireOp",EDGE,"E84.bottom")])]});
            var sketch = newSketch(context, id + "F22", { "sketchPlane" : qUnion([Q0])});
            skLineSegment(sketch, "E113.bottom", {"start": v(-40, -35) * mm, "end": v(-20, -35) * mm});
            skLineSegment(sketch, "E113.top", {"start": v(-40, 10) * mm, "end": v(-20, 10) * mm});
            skLineSegment(sketch, "E113.left", {"start": v(-40, -35) * mm, "end": v(-40, 10) * mm});
            skLineSegment(sketch, "E113.right", {"start": v(-20, -35) * mm, "end": v(-20, 10) * mm});
            skLineSegment(sketch, "E114.bottom", {"start": v(40, -35) * mm, "end": v(20, -35) * mm});
            skLineSegment(sketch, "E114.top", {"start": v(40, 10) * mm, "end": v(20, 10) * mm});
            skLineSegment(sketch, "E114.left", {"start": v(40, -35) * mm, "end": v(40, 10) * mm});
            skLineSegment(sketch, "E114.right", {"start": v(20, -35) * mm, "end": v(20, 10) * mm});
            skSolve(sketch);
        }
        {
            var Q0;
            Q0 = qSketchRegion(id + "F22", true);
            extrude(context, id + "F23", {"entities" : qUnion([Q0]), "depth" : 12.5 * mm});
        }
        {
            var Q0;
            Q0=makeQuery(id+"F19.opExtrude","CAP_FACE",FACE,{"disambiguationData":[OSD([sQuery(id+"F17.wireOp",EDGE,"E84.bottom"),sQuery(id+"F17.wireOp",EDGE,"E84.top"),sQuery(id+"F17.wireOp",EDGE,"E84.left"),sQuery(id+"F17.wireOp",EDGE,"E84.right"),sQuery(id+"F17.wireOp",EDGE,"E86.left")])],"isStart":false});
            var sketch = newSketch(context, id + "F24", { "sketchPlane" : qUnion([Q0])});
            skLineSegment(sketch, "E115.bottom", {"start": v(-40, 12.5) * mm, "end": v(40, 12.5) * mm});
            skLineSegment(sketch, "E115.top", {"start": v(-40, -25) * mm, "end": v(40, -25) * mm});
            skLineSegment(sketch, "E115.left", {"start": v(-40, 12.5) * mm, "end": v(-40, -25) * mm});
            skLineSegment(sketch, "E115.right", {"start": v(40, 12.5) * mm, "end": v(40, -25) * mm});
            skSolve(sketch);
        }
        {
            var Q0;
            Q0 = qSketchRegion(id + "F24", true);
            extrude(context, id + "F25", {"entities" : qUnion([Q0]), "depth" : 12.5 * mm});
        }
        {
            var Q0;
            Q0=makeQuery(id+"F25.opExtrude","CAP_FACE",FACE,{"disambiguationData":[OSD([sQuery(id+"F24.wireOp",EDGE,"E115.bottom"),sQuery(id+"F24.wireOp",EDGE,"E115.top"),sQuery(id+"F24.wireOp",EDGE,"E115.left"),sQuery(id+"F24.wireOp",EDGE,"E115.right")])],"isStart":true});
            var sketch = newSketch(context, id + "F26", { "sketchPlane" : qUnion([Q0])});
            skCircle(sketch, "E116", {"center": v(30, 6.25) * mm, "radius": 3.3 * mm});
            skCircle(sketch, "E117", {"center": v(33.75, -12.5) * mm, "radius": 3.3 * mm});
            skCircle(sketch, "E118", {"center": v(-30, 6.25) * mm, "radius": 3.3 * mm});
            skCircle(sketch, "E119", {"center": v(-33.75, -12.5) * mm, "radius": 3.3 * mm});
            skCircle(sketch, "E120", {"center": v(30, 6.25) * mm, "radius": 2.5 * mm});
            skCircle(sketch, "E121", {"center": v(33.75, -12.5) * mm, "radius": 2.5 * mm});
            skCircle(sketch, "E122", {"center": v(-33.75, -12.5) * mm, "radius": 2.5 * mm});
            skCircle(sketch, "E123", {"center": v(-30, 6.25) * mm, "radius": 2.5 * mm});
            skLineSegment(sketch, "E124", {"start": v(27.5, -25) * mm, "end": v(40, 0) * mm, "construction": true});
            skLineSegment(sketch, "E125", {"start": v(0, 0) * mm, "end": v(0, -25) * mm, "construction": true});
            skLineSegment(sketch, "E126", {"start": v(40, 0) * mm, "end": v(20, 12.5) * mm, "construction": true});
            skCircle(sketch, "E127", {"center": v(13.75, -18.75) * mm, "radius": 2.5 * mm});
            skCircle(sketch, "E128", {"center": v(13.75, -18.75) * mm, "radius": 3.3 * mm});
            skLineSegment(sketch, "E129", {"start": v(27.5, -25) * mm, "end": v(0, -12.5) * mm, "construction": true});
            skCircle(sketch, "E130.MirrorC", {"center": v(-13.75, -18.75) * mm, "radius": 2.5 * mm});
            skCircle(sketch, "E131.MirrorC", {"center": v(-13.75, -18.75) * mm, "radius": 3.3 * mm});
            skLineSegment(sketch, "E132", {"start": v(10, -12.5) * mm, "end": v(-10, 0) * mm, "construction": true});
            skCircle(sketch, "E133", {"center": v(0, -6.25) * mm, "radius": 6 * mm});
            skCircle(sketch, "E134", {"center": v(0, -6.25) * mm, "radius": 5 * mm});
            skCircle(sketch, "E135", {"center": v(0, -6.25) * mm, "radius": 2.5 * mm});
            skSolve(sketch);
        }
        {
            var Q0;
            Q0=makeQuery(id+"F26.imprint","IMPRINT",FACE,{"disambiguationData":[TD([[makeQuery(id+"F26.imprint","IMPRINT",EDGE,{"derivedFrom":sQuery(id+"F26.wireOp",EDGE,"E120")}),1.0]])]});
            var Q1;
            Q1=makeQuery(id+"F26.imprint","IMPRINT",FACE,{"disambiguationData":[TD([[makeQuery(id+"F26.imprint","IMPRINT",EDGE,{"derivedFrom":sQuery(id+"F26.wireOp",EDGE,"E121")}),1.0]])]});
            var Q2;
            Q2=makeQuery(id+"F26.imprint","IMPRINT",FACE,{"disambiguationData":[TD([[makeQuery(id+"F26.imprint","IMPRINT",EDGE,{"derivedFrom":sQuery(id+"F26.wireOp",EDGE,"E122")}),1.0]])]});
            var Q3;
            Q3=makeQuery(id+"F26.imprint","IMPRINT",FACE,{"disambiguationData":[TD([[makeQuery(id+"F26.imprint","IMPRINT",EDGE,{"derivedFrom":sQuery(id+"F26.wireOp",EDGE,"E123")}),1.0]])]});
            var Q4;
            Q4=makeQuery(id+"F26.imprint","IMPRINT",FACE,{"disambiguationData":[TD([[makeQuery(id+"F26.imprint","IMPRINT",EDGE,{"derivedFrom":sQuery(id+"F26.wireOp",EDGE,"E127")}),1.0]])]});
            var Q5;
            Q5=makeQuery(id+"F26.imprint","IMPRINT",FACE,{"disambiguationData":[TD([[makeQuery(id+"F26.imprint","IMPRINT",EDGE,{"derivedFrom":sQuery(id+"F26.wireOp",EDGE,"E130.MirrorC")}),-1.0]])]});
            extrude(context, id + "F27", {"entities" : qUnion([Q0, Q1, Q2, Q3, Q4, Q5]), "operationType" : NewBodyOperationType.REMOVE, "depth" : 25 * mm});
        }
        {
            var Q0;
            Q0=makeQuery(id+"F26.imprint","IMPRINT",FACE,{"disambiguationData":[TD([[makeQuery(id+"F26.imprint","IMPRINT",EDGE,{"derivedFrom":sQuery(id+"F26.wireOp",EDGE,"E116")}),1.0]])]});
            var Q1;
            Q1=makeQuery(id+"F26.imprint","IMPRINT",FACE,{"disambiguationData":[TD([[makeQuery(id+"F26.imprint","IMPRINT",EDGE,{"derivedFrom":sQuery(id+"F26.wireOp",EDGE,"E120")}),1.0]])]});
            var Q2;
            Q2=makeQuery(id+"F26.imprint","IMPRINT",FACE,{"disambiguationData":[TD([[makeQuery(id+"F26.imprint","IMPRINT",EDGE,{"derivedFrom":sQuery(id+"F26.wireOp",EDGE,"E117")}),1.0]])]});
            var Q3;
            Q3=makeQuery(id+"F26.imprint","IMPRINT",FACE,{"disambiguationData":[TD([[makeQuery(id+"F26.imprint","IMPRINT",EDGE,{"derivedFrom":sQuery(id+"F26.wireOp",EDGE,"E121")}),1.0]])]});
            var Q4;
            Q4=makeQuery(id+"F26.imprint","IMPRINT",FACE,{"disambiguationData":[TD([[makeQuery(id+"F26.imprint","IMPRINT",EDGE,{"derivedFrom":sQuery(id+"F26.wireOp",EDGE,"E122")}),1.0]])]});
            var Q5;
            Q5=makeQuery(id+"F26.imprint","IMPRINT",FACE,{"disambiguationData":[TD([[makeQuery(id+"F26.imprint","IMPRINT",EDGE,{"derivedFrom":sQuery(id+"F26.wireOp",EDGE,"E119")}),1.0]])]});
            var Q6;
            Q6=makeQuery(id+"F26.imprint","IMPRINT",FACE,{"disambiguationData":[TD([[makeQuery(id+"F26.imprint","IMPRINT",EDGE,{"derivedFrom":sQuery(id+"F26.wireOp",EDGE,"E123")}),1.0]])]});
            var Q7;
            Q7=makeQuery(id+"F26.imprint","IMPRINT",FACE,{"disambiguationData":[TD([[makeQuery(id+"F26.imprint","IMPRINT",EDGE,{"derivedFrom":sQuery(id+"F26.wireOp",EDGE,"E118")}),1.0]])]});
            var Q8;
            Q8=makeQuery(id+"F26.imprint","IMPRINT",FACE,{"disambiguationData":[TD([[makeQuery(id+"F26.imprint","IMPRINT",EDGE,{"derivedFrom":sQuery(id+"F26.wireOp",EDGE,"E127")}),1.0]])]});
            var Q9;
            Q9=makeQuery(id+"F26.imprint","IMPRINT",FACE,{"disambiguationData":[TD([[makeQuery(id+"F26.imprint","IMPRINT",EDGE,{"derivedFrom":sQuery(id+"F26.wireOp",EDGE,"E127")}),-1.0]])]});
            var Q10;
            Q10=makeQuery(id+"F26.imprint","IMPRINT",FACE,{"disambiguationData":[TD([[makeQuery(id+"F26.imprint","IMPRINT",EDGE,{"derivedFrom":sQuery(id+"F26.wireOp",EDGE,"E130.MirrorC")}),-1.0]])]});
            var Q11;
            Q11=makeQuery(id+"F26.imprint","IMPRINT",FACE,{"disambiguationData":[TD([[makeQuery(id+"F26.imprint","IMPRINT",EDGE,{"derivedFrom":sQuery(id+"F26.wireOp",EDGE,"E130.MirrorC")}),1.0]])]});
            var Q12;
            Q12=makeQuery(id+"F26.imprint","IMPRINT",FACE,{"disambiguationData":[TD([[makeQuery(id+"F26.imprint","IMPRINT",EDGE,{"derivedFrom":sQuery(id+"F26.wireOp",EDGE,"E134")}),1.0]])]});
            var Q13;
            Q13=makeQuery(id+"F26.imprint","IMPRINT",FACE,{"disambiguationData":[TD([[makeQuery(id+"F26.imprint","IMPRINT",EDGE,{"derivedFrom":sQuery(id+"F26.wireOp",EDGE,"E135")}),1.0]])]});
            var Q14;
            Q14=sQuery(id+"F26.wireOp",EDGE,"E116");
            var Q15;
            Q15=sQuery(id+"F26.wireOp",EDGE,"E117");
            var Q16;
            Q16=sQuery(id+"F26.wireOp",EDGE,"E119");
            var Q17;
            Q17=sQuery(id+"F26.wireOp",EDGE,"E118");
            extrude(context, id + "F28", {"entities" : qUnion([Q0, Q1, Q2, Q3, Q4, Q5, Q6, Q7, Q8, Q9, Q10, Q11, Q12, Q13]), "operationType" : NewBodyOperationType.REMOVE, "surfaceEntities" : qUnion([Q14, Q15, Q16, Q17]), "endBound" : BoundingType.THROUGH_ALL, "oppositeDirection" : true, "depth" : 25 * mm});
        }
        {
            var Q0;
            Q0=makeQuery(id+"F18.opExtrude","SWEPT_FACE",FACE,{"disambiguationData":[OSD([sQuery(id+"F17.wireOp",EDGE,"E84.bottom")])]});
            var sketch = newSketch(context, id + "F29", { "sketchPlane" : qUnion([Q0])});
            skCircle(sketch, "E136", {"center": v(-33.75, -5) * mm, "radius": 2.5 * mm});
            skCircle(sketch, "E137", {"center": v(-33.75, -5) * mm, "radius": 3.3 * mm});
            skLineSegment(sketch, "E138", {"start": v(-40, 25) * mm, "end": v(-27.5, -35) * mm, "construction": true});
            skCircle(sketch, "E139.MirrorC", {"center": v(33.75, -5) * mm, "radius": 3.3 * mm});
            skCircle(sketch, "E140.MirrorC", {"center": v(33.75, -5) * mm, "radius": 2.5 * mm});
            skSolve(sketch);
        }
        {
            var Q0;
            Q0=makeQuery(id+"F29.imprint","IMPRINT",FACE,{"disambiguationData":[TD([[makeQuery(id+"F29.imprint","IMPRINT",EDGE,{"derivedFrom":sQuery(id+"F29.wireOp",EDGE,"E136")}),1.0]])]});
            var Q1;
            Q1=makeQuery(id+"F29.imprint","IMPRINT",FACE,{"disambiguationData":[TD([[makeQuery(id+"F29.imprint","IMPRINT",EDGE,{"derivedFrom":sQuery(id+"F29.wireOp",EDGE,"E140.MirrorC")}),-1.0]])]});
            extrude(context, id + "F30", {"entities" : qUnion([Q0, Q1]), "operationType" : NewBodyOperationType.REMOVE, "oppositeDirection" : true, "depth" : 25 * mm});
        }
        {
            var Q0;
            Q0=makeQuery(id+"F29.imprint","IMPRINT",FACE,{"disambiguationData":[TD([[makeQuery(id+"F29.imprint","IMPRINT",EDGE,{"derivedFrom":sQuery(id+"F29.wireOp",EDGE,"E136")}),1.0]])]});
            var Q1;
            Q1=makeQuery(id+"F29.imprint","IMPRINT",FACE,{"disambiguationData":[TD([[makeQuery(id+"F29.imprint","IMPRINT",EDGE,{"derivedFrom":sQuery(id+"F29.wireOp",EDGE,"E136")}),-1.0]])]});
            var Q2;
            Q2=makeQuery(id+"F29.imprint","IMPRINT",FACE,{"disambiguationData":[TD([[makeQuery(id+"F29.imprint","IMPRINT",EDGE,{"derivedFrom":sQuery(id+"F29.wireOp",EDGE,"E140.MirrorC")}),-1.0]])]});
            var Q3;
            Q3=makeQuery(id+"F29.imprint","IMPRINT",FACE,{"disambiguationData":[TD([[makeQuery(id+"F29.imprint","IMPRINT",EDGE,{"derivedFrom":sQuery(id+"F29.wireOp",EDGE,"E139.MirrorC")}),-1.0]])]});
            extrude(context, id + "F31", {"entities" : qUnion([Q0, Q1, Q2, Q3]), "operationType" : NewBodyOperationType.REMOVE, "endBound" : BoundingType.THROUGH_ALL, "depth" : 25 * mm});
        }
        {
            var Q0;
            Q0=makeQuery(id+"F17.imprint","IMPRINT",FACE,{"disambiguationData":[TD([[makeQuery(id+"F17.imprint","IMPRINT",EDGE,{"derivedFrom":sQuery(id+"F17.wireOp",EDGE,"E87")}),1.0]])]});
            var Q1;
            Q1=makeQuery(id+"F17.imprint","IMPRINT",FACE,{"disambiguationData":[TD([[makeQuery(id+"F17.imprint","IMPRINT",EDGE,{"derivedFrom":sQuery(id+"F17.wireOp",EDGE,"E87")}),-1.0]])]});
            var Q2;
            Q2=makeQuery(id+"F17.imprint","IMPRINT",FACE,{"disambiguationData":[TD([[makeQuery(id+"F17.imprint","IMPRINT",EDGE,{"derivedFrom":sQuery(id+"F17.wireOp",EDGE,"E91.MirrorC")}),-1.0]])]});
            var Q3;
            Q3=makeQuery(id+"F17.imprint","IMPRINT",FACE,{"disambiguationData":[TD([[makeQuery(id+"F17.imprint","IMPRINT",EDGE,{"derivedFrom":sQuery(id+"F17.wireOp",EDGE,"E90.MirrorC")}),-1.0]])]});
            var Q4;
            Q4=makeQuery(id+"F17.imprint","IMPRINT",FACE,{"disambiguationData":[TD([[makeQuery(id+"F17.imprint","IMPRINT",EDGE,{"derivedFrom":sQuery(id+"F17.wireOp",EDGE,"E97")}),1.0]])]});
            var Q5;
            Q5=makeQuery(id+"F17.imprint","IMPRINT",FACE,{"disambiguationData":[TD([[makeQuery(id+"F17.imprint","IMPRINT",EDGE,{"derivedFrom":sQuery(id+"F17.wireOp",EDGE,"E97")}),-1.0]])]});
            var Q6;
            Q6=makeQuery(id+"F17.imprint","IMPRINT",FACE,{"disambiguationData":[TD([[makeQuery(id+"F17.imprint","IMPRINT",EDGE,{"derivedFrom":sQuery(id+"F17.wireOp",EDGE,"jnnbCi9O-ACNy-IIGJ-mOF9-m1iE8Juj3V3K")}),1.0]])]});
            var Q7;
            Q7=makeQuery(id+"F17.imprint","IMPRINT",FACE,{"disambiguationData":[TD([[makeQuery(id+"F17.imprint","IMPRINT",EDGE,{"derivedFrom":sQuery(id+"F17.wireOp",EDGE,"jnnbCi9O-ACNy-IIGJ-mOF9-m1iE8Juj3V3K")}),-1.0]])]});
            var Q8;
            Q8=makeQuery(id+"F17.imprint","IMPRINT",FACE,{"disambiguationData":[TD([[makeQuery(id+"F17.imprint","IMPRINT",EDGE,{"derivedFrom":sQuery(id+"F17.wireOp",EDGE,"E99.MirrorC")}),-1.0]])]});
            var Q9;
            Q9=makeQuery(id+"F17.imprint","IMPRINT",FACE,{"disambiguationData":[TD([[makeQuery(id+"F17.imprint","IMPRINT",EDGE,{"derivedFrom":sQuery(id+"F17.wireOp",EDGE,"E99.MirrorC")}),1.0]])]});
            var Q10;
            Q10=makeQuery(id+"F17.imprint","IMPRINT",FACE,{"disambiguationData":[TD([[makeQuery(id+"F17.imprint","IMPRINT",EDGE,{"derivedFrom":sQuery(id+"F17.wireOp",EDGE,"E92.MirrorC")}),1.0]])]});
            var Q11;
            Q11=makeQuery(id+"F17.imprint","IMPRINT",FACE,{"disambiguationData":[TD([[makeQuery(id+"F17.imprint","IMPRINT",EDGE,{"derivedFrom":sQuery(id+"F17.wireOp",EDGE,"E92.MirrorC")}),-1.0]])]});
            var Q12;
            Q12=makeQuery(id+"F17.imprint","IMPRINT",FACE,{"disambiguationData":[TD([[makeQuery(id+"F17.imprint","IMPRINT",EDGE,{"derivedFrom":sQuery(id+"F17.wireOp",EDGE,"E94.MirrorC")}),1.0]])]});
            var Q13;
            Q13=makeQuery(id+"F17.imprint","IMPRINT",FACE,{"disambiguationData":[TD([[makeQuery(id+"F17.imprint","IMPRINT",EDGE,{"derivedFrom":sQuery(id+"F17.wireOp",EDGE,"E95.MirrorC")}),1.0]])]});
            extrude(context, id + "F32", {"entities" : qUnion([Q0, Q1, Q2, Q3, Q4, Q5, Q6, Q7, Q8, Q9, Q10, Q11, Q12, Q13]), "operationType" : NewBodyOperationType.REMOVE, "endBound" : BoundingType.THROUGH_ALL, "oppositeDirection" : true, "depth" : 25 * mm});
        }
        {
            var Q0;
            Q0=makeQuery(id+"F17.imprint","IMPRINT",FACE,{"disambiguationData":[TD([[makeQuery(id+"F17.imprint","IMPRINT",EDGE,{"derivedFrom":sQuery(id+"F17.wireOp",EDGE,"E97")}),1.0]])]});
            var Q1;
            Q1=makeQuery(id+"F17.imprint","IMPRINT",FACE,{"disambiguationData":[TD([[makeQuery(id+"F17.imprint","IMPRINT",EDGE,{"derivedFrom":sQuery(id+"F17.wireOp",EDGE,"jnnbCi9O-ACNy-IIGJ-mOF9-m1iE8Juj3V3K")}),1.0]])]});
            var Q2;
            Q2=makeQuery(id+"F17.imprint","IMPRINT",FACE,{"disambiguationData":[TD([[makeQuery(id+"F17.imprint","IMPRINT",EDGE,{"derivedFrom":sQuery(id+"F17.wireOp",EDGE,"E91.MirrorC")}),-1.0]])]});
            var Q3;
            Q3=makeQuery(id+"F17.imprint","IMPRINT",FACE,{"disambiguationData":[TD([[makeQuery(id+"F17.imprint","IMPRINT",EDGE,{"derivedFrom":sQuery(id+"F17.wireOp",EDGE,"E87")}),1.0]])]});
            var Q4;
            Q4=makeQuery(id+"F17.imprint","IMPRINT",FACE,{"disambiguationData":[TD([[makeQuery(id+"F17.imprint","IMPRINT",EDGE,{"derivedFrom":sQuery(id+"F17.wireOp",EDGE,"E99.MirrorC")}),-1.0]])]});
            var Q5;
            Q5=makeQuery(id+"F17.imprint","IMPRINT",FACE,{"disambiguationData":[TD([[makeQuery(id+"F17.imprint","IMPRINT",EDGE,{"derivedFrom":sQuery(id+"F17.wireOp",EDGE,"E95.MirrorC")}),1.0]])]});
            var Q6;
            Q6=makeQuery(id+"F17.imprint","IMPRINT",FACE,{"disambiguationData":[TD([[makeQuery(id+"F17.imprint","IMPRINT",EDGE,{"derivedFrom":sQuery(id+"F17.wireOp",EDGE,"E92.MirrorC")}),-1.0]])]});
            extrude(context, id + "F33", {"entities" : qUnion([Q0, Q1, Q2, Q3, Q4, Q5, Q6]), "operationType" : NewBodyOperationType.REMOVE, "depth" : 25 * mm});
        }
        {
            var Q0;
            Q0=makeQuery(id+"F21.opExtrude","SWEPT_FACE",FACE,{"disambiguationData":[OSD([sQuery(id+"F20.wireOp",EDGE,"E110")])]});
            var sketch = newSketch(context, id + "F34", { "sketchPlane" : qUnion([Q0])});
            skLineSegment(sketch, "E141", {"start": v(-10, -12.5) * mm, "end": v(10, 0) * mm, "construction": true});
            skCircle(sketch, "E142", {"center": v(0, -6.25) * mm, "radius": 4 * mm});
            skSolve(sketch);
        }
        {
            var Q0;
            Q0=makeQuery(id+"F34.imprint","IMPRINT",FACE,{"disambiguationData":[TD([[makeQuery(id+"F34.imprint","IMPRINT",EDGE,{"derivedFrom":sQuery(id+"F34.wireOp",EDGE,"E142")}),1.0]])]});
            extrude(context, id + "F35", {"entities" : qUnion([Q0]), "oppositeDirection" : true, "depth" : 10 * mm});
        }
        {
            var Q0;
            Q0=makeQuery(id+"F35.opExtrude","SWEPT_BODY",BODY,{"disambiguationData":[OSD([sQuery(id+"F34.wireOp",EDGE,"E142")])]});
            var Q1;
            Q1=makeQuery(id+"F21.opExtrude","SWEPT_BODY",BODY,{"disambiguationData":[OSD([sQuery(id+"F20.wireOp",EDGE,"E103.right"),sQuery(id+"F20.wireOp",EDGE,"E104"),sQuery(id+"F20.wireOp",EDGE,"E105"),sQuery(id+"F20.wireOp",EDGE,"E108"),sQuery(id+"F20.wireOp",EDGE,"E109"),sQuery(id+"F20.wireOp",EDGE,"E110"),sQuery(id+"F20.wireOp",EDGE,"E111"),sQuery(id+"F20.wireOp",EDGE,"E112")])]});
            booleanBodies(context, id + "F36", {"operationType" : BooleanOperationType.SUBTRACTION, "tools" : qUnion([Q0]), "targets" : qUnion([Q1]), "keepTools" : true});
        }
        {
            var Q0;
            Q0=makeQuery(id+"F26.imprint","IMPRINT",FACE,{"disambiguationData":[TD([[makeQuery(id+"F26.imprint","IMPRINT",EDGE,{"derivedFrom":sQuery(id+"F26.wireOp",EDGE,"E134")}),1.0]])]});
            var Q1;
            Q1=makeQuery(id+"F25.opExtrude","CAP_FACE",FACE,{"disambiguationData":[OSD([sQuery(id+"F24.wireOp",EDGE,"E115.bottom"),sQuery(id+"F24.wireOp",EDGE,"E115.top"),sQuery(id+"F24.wireOp",EDGE,"E115.left"),sQuery(id+"F24.wireOp",EDGE,"E115.right")])],"isStart":false});
            extrude(context, id + "F37", {"entities" : qUnion([Q0]), "oppositeDirection" : true, "endBoundEntityFace" : qUnion([Q1]), "depth" : 14.5 * mm});
        }
        {
            var Q0;
            Q0=makeQuery(id+"F26.imprint","IMPRINT",FACE,{"disambiguationData":[TD([[makeQuery(id+"F26.imprint","IMPRINT",EDGE,{"derivedFrom":sQuery(id+"F26.wireOp",EDGE,"E134")}),1.0]])]});
            var Q1;
            Q1=makeQuery(id+"F26.imprint","IMPRINT",FACE,{"disambiguationData":[TD([[makeQuery(id+"F26.imprint","IMPRINT",EDGE,{"derivedFrom":sQuery(id+"F26.wireOp",EDGE,"E133")}),1.0]])]});
            extrude(context, id + "F38", {"entities" : qUnion([Q0, Q1]), "operationType" : NewBodyOperationType.ADD, "depth" : 2 * mm});
        }
        {
            var Q0;
            Q0=makeQuery(id+"F3.opExtrude","CAP_FACE",FACE,{"disambiguationData":[OSD([sQuery(id+"F2.wireOp",EDGE,"E0.bottom"),sQuery(id+"F2.wireOp",EDGE,"E1.top"),sQuery(id+"F2.wireOp",EDGE,"E1.left"),sQuery(id+"F2.wireOp",EDGE,"E1.right")])],"isStart":true});
            var sketch = newSketch(context, id + "F39", { "sketchPlane" : qUnion([Q0])});
            skCircle(sketch, "E143", {"center": v(20, 31.25) * mm, "radius": 5 * mm});
            skCircle(sketch, "E144", {"center": v(-20, 31.25) * mm, "radius": 5 * mm});
            skCircle(sketch, "E145", {"center": v(0, 1.25) * mm, "radius": 5 * mm});
            skCircle(sketch, "E146", {"center": v(0, 1.25) * mm, "radius": 3.15 * mm});
            skCircle(sketch, "E147", {"center": v(20, 31.25) * mm, "radius": 2.5 * mm});
            skCircle(sketch, "E148", {"center": v(-20, 31.25) * mm, "radius": 2.5 * mm});
            skSolve(sketch);
        }
        {
            var Q0;
            Q0=makeQuery(id+"F39.imprint","IMPRINT",FACE,{"disambiguationData":[TD([[makeQuery(id+"F39.imprint","IMPRINT",EDGE,{"derivedFrom":sQuery(id+"F39.wireOp",EDGE,"E144")}),1.0]])]});
            var Q1;
            Q1=makeQuery(id+"F16.opPattern","COPY",FACE,{"derivedFrom":makeQuery(id+"F11.opRevolve","SWEPT_FACE",FACE,{"disambiguationData":[OSD([sQuery(id+"F4.wireOp",EDGE,"E75")])]}),"instanceName":"1"});
            extrude(context, id + "F40", {"entities" : qUnion([Q0]), "operationType" : NewBodyOperationType.REMOVE, "endBound" : BoundingType.UP_TO_SURFACE, "oppositeDirection" : true, "endBoundEntityFace" : qUnion([Q1]), "depth" : 25 * mm});
        }
        {
            var Q0;
            Q0=makeQuery(id+"F39.imprint","IMPRINT",FACE,{"disambiguationData":[TD([[makeQuery(id+"F39.imprint","IMPRINT",EDGE,{"derivedFrom":sQuery(id+"F39.wireOp",EDGE,"E143")}),1.0]])]});
            var Q1;
            Q1=makeQuery(id+"F11.opRevolve","SWEPT_FACE",FACE,{"disambiguationData":[OSD([sQuery(id+"F4.wireOp",EDGE,"E75")])]});
            extrude(context, id + "F41", {"entities" : qUnion([Q0]), "operationType" : NewBodyOperationType.REMOVE, "endBound" : BoundingType.UP_TO_SURFACE, "oppositeDirection" : true, "endBoundEntityFace" : qUnion([Q1]), "depth" : 25 * mm});
        }
        {
            var Q0;
            Q0=makeQuery(id+"F39.imprint","IMPRINT",FACE,{"disambiguationData":[TD([[makeQuery(id+"F39.imprint","IMPRINT",EDGE,{"derivedFrom":sQuery(id+"F39.wireOp",EDGE,"E145")}),1.0]])]});
            var Q1;
            Q1=makeQuery(id+"F10.opRevolve","SWEPT_FACE",FACE,{"disambiguationData":[OSD([sQuery(id+"F4.wireOp",EDGE,"E72")])]});
            extrude(context, id + "F42", {"entities" : qUnion([Q0]), "operationType" : NewBodyOperationType.REMOVE, "endBound" : BoundingType.UP_TO_SURFACE, "oppositeDirection" : true, "endBoundEntityFace" : qUnion([Q1]), "depth" : 25 * mm});
        }
        {
            var Q0;
            Q0=makeQuery(id+"F39.imprint","IMPRINT",FACE,{"disambiguationData":[TD([[makeQuery(id+"F39.imprint","IMPRINT",EDGE,{"derivedFrom":sQuery(id+"F39.wireOp",EDGE,"E147")}),1.0]])]});
            var Q1;
            Q1=makeQuery(id+"F39.imprint","IMPRINT",FACE,{"disambiguationData":[TD([[makeQuery(id+"F39.imprint","IMPRINT",EDGE,{"derivedFrom":sQuery(id+"F39.wireOp",EDGE,"E148")}),1.0]])]});
            var Q2;
            Q2=sQuery(id+"F39.wireOp",EDGE,"E147");
            extrude(context, id + "F43", {"entities" : qUnion([Q0, Q1]), "operationType" : NewBodyOperationType.REMOVE, "surfaceEntities" : qUnion([Q2]), "oppositeDirection" : true, "depth" : 25 * mm});
        }
        {
            var Q0;
            Q0=makeQuery(id+"F39.imprint","IMPRINT",FACE,{"disambiguationData":[TD([[makeQuery(id+"F39.imprint","IMPRINT",EDGE,{"derivedFrom":sQuery(id+"F39.wireOp",EDGE,"E146")}),1.0]])]});
            var Q1;
            Q1=sQuery(id+"F39.wireOp",EDGE,"E146");
            extrude(context, id + "F44", {"entities" : qUnion([Q0]), "operationType" : NewBodyOperationType.REMOVE, "surfaceEntities" : qUnion([Q1]), "endBound" : BoundingType.THROUGH_ALL, "oppositeDirection" : true, "depth" : 25 * mm});
        }
        {
            var Q0;
            Q0=makeQuery(id+"F44.boolean.opBoolean","INTERSECT",EDGE,{"derivedFrom":[makeQuery(id+"F21.opExtrude","CAP_FACE",FACE,{"disambiguationData":[OSD([sQuery(id+"F20.wireOp",EDGE,"E103.right"),sQuery(id+"F20.wireOp",EDGE,"E104"),sQuery(id+"F20.wireOp",EDGE,"E105"),sQuery(id+"F20.wireOp",EDGE,"E108"),sQuery(id+"F20.wireOp",EDGE,"E109"),sQuery(id+"F20.wireOp",EDGE,"E110"),sQuery(id+"F20.wireOp",EDGE,"E111"),sQuery(id+"F20.wireOp",EDGE,"E112")])],"isStart":false}),makeQuery(id+"F44.opExtrude","SWEPT_FACE",FACE,{"disambiguationData":[OSD([sQuery(id+"F39.wireOp",EDGE,"E146")])]})]});
            chamfer(context, id + "F45", {"entities" : qUnion([Q0]), "width" : (getVariable(context, 'M6cap') - getVariable(context, 'M6clear')) / 2 * mm, "tangentPropagation" : true});
        }
        {
            var Q0;
            Q0=makeQuery(id+"F10.opRevolve","SWEPT_FACE",FACE,{"disambiguationData":[OSD([sQuery(id+"F4.wireOp",EDGE,"E76.top")])]});
            var sketch = newSketch(context, id + "F46", { "sketchPlane" : qUnion([Q0])});
            skLineSegment(sketch, "E149", {"start": v(-4.5, 1.25) * mm, "end": v(4.5, 1.25) * mm, "construction": true});
            skPoint(sketch, "E150", {"position": v(0, 1.25) * mm});
            skCircle(sketch, "E151", {"center": v(0, 1.25) * mm, "radius": 1 * mm});
            skCircle(sketch, "E152", {"center": v(3, 1.25) * mm, "radius": 1 * mm});
            skCircle(sketch, "E153", {"center": v(-3, 1.25) * mm, "radius": 1 * mm});
            skSolve(sketch);
        }
        {
            var Q0;
            Q0=makeQuery(id+"F46.imprint","IMPRINT",FACE,{"disambiguationData":[TD([[makeQuery(id+"F46.imprint","IMPRINT",EDGE,{"derivedFrom":sQuery(id+"F46.wireOp",EDGE,"E153")}),1.0]])]});
            var Q1;
            Q1=makeQuery(id+"F46.imprint","IMPRINT",FACE,{"disambiguationData":[TD([[makeQuery(id+"F46.imprint","IMPRINT",EDGE,{"derivedFrom":sQuery(id+"F46.wireOp",EDGE,"E152")}),1.0]])]});
            extrude(context, id + "F47", {"entities" : qUnion([Q0, Q1]), "operationType" : NewBodyOperationType.REMOVE, "oppositeDirection" : true, "depth" : 3 * mm});
        }
        {
            var Q0;
            Q0=makeQuery(id+"F46.imprint","IMPRINT",FACE,{"disambiguationData":[TD([[makeQuery(id+"F46.imprint","IMPRINT",EDGE,{"derivedFrom":sQuery(id+"F46.wireOp",EDGE,"E151")}),1.0]])]});
            extrude(context, id + "F48", {"entities" : qUnion([Q0]), "operationType" : NewBodyOperationType.REMOVE, "endBound" : BoundingType.THROUGH_ALL, "oppositeDirection" : true, "depth" : 5 * mm});
        }
        {
            var Q0;
            Q0=qCreatedBy(makeId("Right.planeOp"),FACE);
            var sketch = newSketch(context, id + "F49", { "sketchPlane" : qUnion([Q0])});
            skLineSegment(sketch, "E154", {"start": v(11.06, 23) * mm, "end": v(-8.56, 23) * mm, "construction": true});
            skLineSegment(sketch, "E155", {"start": v(1.25, 23) * mm, "end": v(1.25, 18) * mm, "construction": true});
            skCircle(sketch, "E156", {"center": v(1.25, 20.5) * mm, "radius": 1.5 * mm});
            skSolve(sketch);
        }
        {
            var Q0;
            Q0=makeQuery(id+"F49.imprint","IMPRINT",FACE,{"disambiguationData":[TD([[makeQuery(id+"F49.imprint","IMPRINT",EDGE,{"derivedFrom":sQuery(id+"F49.wireOp",EDGE,"E156")}),1.0]])]});
            var Q1;
            Q1=sQuery(id+"F49.wireOp",EDGE,"E156");
            extrude(context, id + "F50", {"entities" : qUnion([Q0]), "operationType" : NewBodyOperationType.REMOVE, "surfaceEntities" : qUnion([Q1]), "endBound" : BoundingType.THROUGH_ALL, "oppositeDirection" : true, "depth" : 25 * mm, "hasSecondDirection" : true, "secondDirectionBound" : SecondDirectionBoundingType.THROUGH_ALL, "secondDirectionOppositeDirection" : false, "secondDirectionDepth" : 25 * mm});
        }
    });
